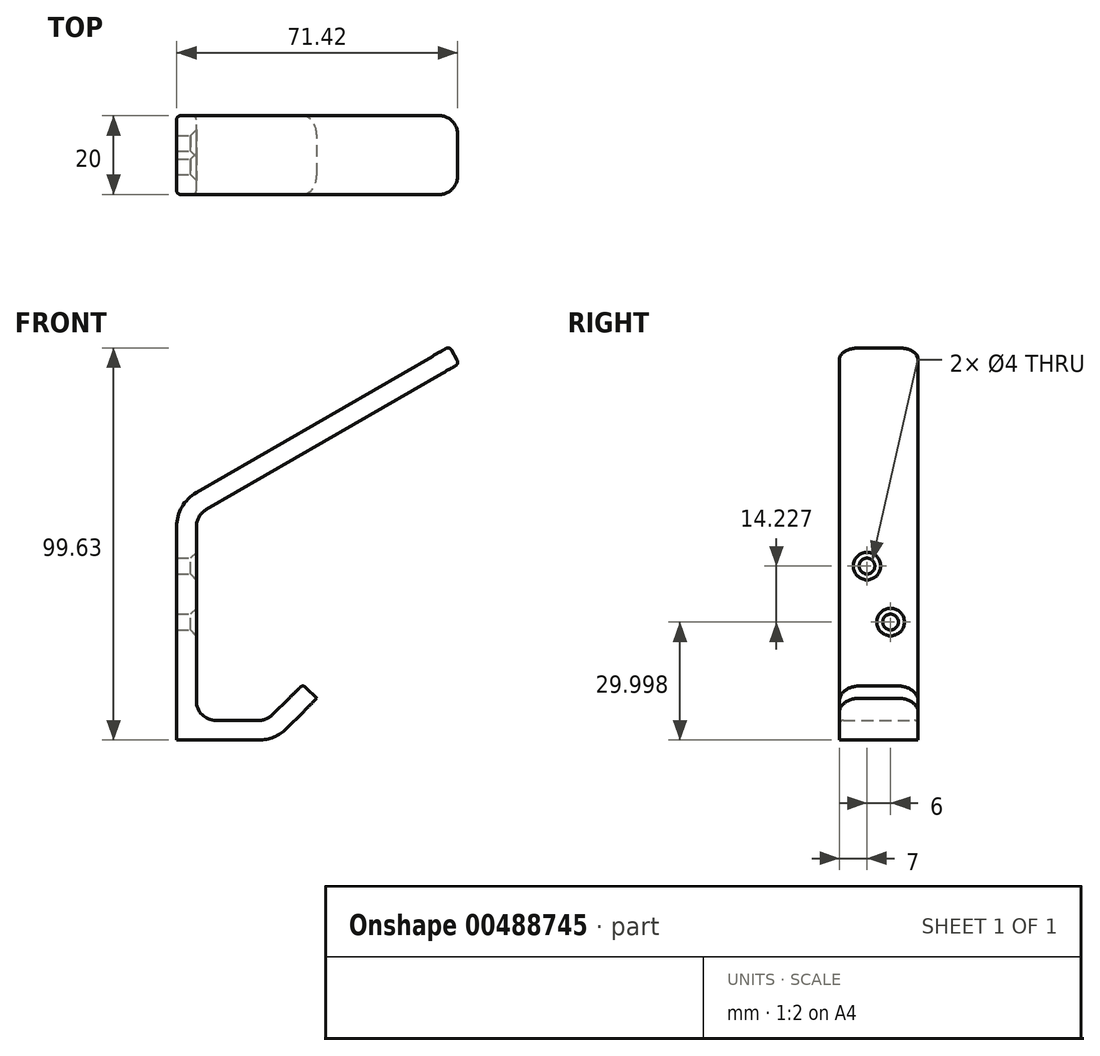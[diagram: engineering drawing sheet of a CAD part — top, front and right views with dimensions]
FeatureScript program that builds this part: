
annotation { "Feature Type Name" : "Feature", "Feature Type Description" : "" }
export const myFeature = defineFeature(function(context is Context, id is Id, definition is map)
    precondition{}
    {
        {
            var Q0;
            Q0=qCreatedBy(makeId("Front.planeOp"),FACE);
            var sketch = newSketch(context, id + "F0", { "sketchPlane" : qUnion([Q0])});
            skLineSegment(sketch, "E0", {"start": v(-35.6, 21.27) * mm, "end": v(-35.6, -38.73) * mm});
            skLineSegment(sketch, "E1", {"start": v(-35.6, 21.27) * mm, "end": v(33.68, 61.27) * mm});
            skLineSegment(sketch, "E2", {"start": v(-35.6, -38.73) * mm, "end": v(-10.6, -38.73) * mm});
            skLineSegment(sketch, "E3", {"start": v(-10.6, -38.73) * mm, "end": v(0, -28.13) * mm});
            skLineSegment(sketch, "E4", {"start": v(0, -28.13) * mm, "end": v(-3.54, -24.59) * mm});
            skLineSegment(sketch, "E5", {"start": v(-3.54, -24.59) * mm, "end": v(-12.68, -33.73) * mm});
            skLineSegment(sketch, "E6", {"start": v(-35.6, -38.73) * mm, "end": v(-35.6, -33.73) * mm});
            skLineSegment(sketch, "E7", {"start": v(-30.6, -33.73) * mm, "end": v(-12.68, -33.73) * mm});
            skLineSegment(sketch, "E8", {"start": v(-35.6, -38.73) * mm, "end": v(-30.6, -38.73) * mm});
            skLineSegment(sketch, "E9", {"start": v(-30.6, -33.73) * mm, "end": v(-30.6, 18.38) * mm});
            skLineSegment(sketch, "E10", {"start": v(33.68, 61.27) * mm, "end": v(36.18, 56.94) * mm});
            skLineSegment(sketch, "E11", {"start": v(36.18, 56.94) * mm, "end": v(-30.6, 18.38) * mm});
            skSolve(sketch);
        }
        {
            var Q0;
            Q0=makeQuery(id+"F0.imprint","IMPRINT",FACE,{"disambiguationData":[TD([[makeQuery(id+"F0.imprint","IMPRINT",EDGE,{"derivedFrom":sQuery(id+"F0.wireOp",EDGE,"E0")}),1.0]])]});
            extrude(context, id + "F1", {"entities" : qUnion([Q0]), "depth" : 20 * mm});
        }
        {
            var Q0;
            Q0=makeQuery(id+"F1.opExtrude","SWEPT_EDGE",EDGE,{"disambiguationData":[OSD([sQuery(id+"F0.wireOp",EDGE,"E0"),sQuery(id+"F0.wireOp",EDGE,"E1")])]});
            fillet(context, id + "F2", {"entities" : qUnion([Q0]), "radius" : 10 * mm, "tangentPropagation" : true, "allowEdgeOverflow" : false});
        }
        {
            var Q0;
            Q0=makeQuery(id+"F1.opExtrude","SWEPT_EDGE",EDGE,{"disambiguationData":[OSD([sQuery(id+"F0.wireOp",EDGE,"E6"),sQuery(id+"F0.wireOp",EDGE,"E8")])]});
            var Q1;
            Q1=makeQuery(id+"F1.opExtrude","SWEPT_EDGE",EDGE,{"disambiguationData":[OSD([sQuery(id+"F0.wireOp",EDGE,"E2"),sQuery(id+"F0.wireOp",EDGE,"E3")])]});
            fillet(context, id + "F3", {"entities" : qUnion([Q0, Q1]), "radius" : 10 * mm, "tangentPropagation" : true, "allowEdgeOverflow" : false});
        }
        {
            var Q0;
            Q0=makeQuery(id+"F1.opExtrude","SWEPT_EDGE",EDGE,{"disambiguationData":[OSD([sQuery(id+"F0.wireOp",EDGE,"E7"),sQuery(id+"F0.wireOp",EDGE,"E9")])]});
            var Q1;
            Q1=makeQuery(id+"F1.opExtrude","SWEPT_EDGE",EDGE,{"disambiguationData":[OSD([sQuery(id+"F0.wireOp",EDGE,"E5"),sQuery(id+"F0.wireOp",EDGE,"E7")])]});
            fillet(context, id + "F4", {"entities" : qUnion([Q0, Q1]), "radius" : 5 * mm, "tangentPropagation" : true, "allowEdgeOverflow" : false});
        }
        {
            var Q0;
            Q0=makeQuery(id+"F1.opExtrude","SWEPT_EDGE",EDGE,{"disambiguationData":[OSD([sQuery(id+"F0.wireOp",EDGE,"E9"),sQuery(id+"F0.wireOp",EDGE,"E11")])]});
            fillet(context, id + "F5", {"entities" : qUnion([Q0]), "radius" : 5 * mm, "tangentPropagation" : true, "allowEdgeOverflow" : false});
        }
        {
            var Q0;
            Q0=makeQuery(id+"F1.opExtrude","CAP_EDGE",EDGE,{"disambiguationData":[OSD([sQuery(id+"F0.wireOp",EDGE,"E4")])],"isStart":true});
            var Q1;
            Q1=makeQuery(id+"F1.opExtrude","CAP_EDGE",EDGE,{"disambiguationData":[OSD([sQuery(id+"F0.wireOp",EDGE,"E4")])],"isStart":false});
            fillet(context, id + "F6", {"entities" : qUnion([Q0, Q1]), "radius" : 5 * mm, "tangentPropagation" : true, "allowEdgeOverflow" : false});
        }
        {
            var Q0;
            Q0=makeQuery(id+"F1.opExtrude","CAP_EDGE",EDGE,{"disambiguationData":[OSD([sQuery(id+"F0.wireOp",EDGE,"E10")])],"isStart":true});
            var Q1;
            Q1=makeQuery(id+"F1.opExtrude","CAP_EDGE",EDGE,{"disambiguationData":[OSD([sQuery(id+"F0.wireOp",EDGE,"E10")])],"isStart":false});
            fillet(context, id + "F7", {"entities" : qUnion([Q0, Q1]), "radius" : 5 * mm, "tangentPropagation" : true, "allowEdgeOverflow" : false});
        }
        {
            var Q0;
            Q0=makeQuery(id+"F1.opExtrude","CAP_EDGE",EDGE,{"disambiguationData":[OSD([sQuery(id+"F0.wireOp",EDGE,"E1")])],"isStart":false});
            var Q1;
            Q1=makeQuery(id+"F1.opExtrude","CAP_EDGE",EDGE,{"disambiguationData":[OSD([sQuery(id+"F0.wireOp",EDGE,"E11")])],"isStart":false});
            var Q2;
            Q2=makeQuery(id+"F7.opFillet","BLEND_EDGE",EDGE,{"blendedFrom":[makeQuery(id+"F1.opExtrude","CAP_EDGE",EDGE,{"disambiguationData":[OSD([sQuery(id+"F0.wireOp",EDGE,"E10")])],"isStart":false}),makeQuery(id+"F1.opExtrude","SWEPT_FACE",FACE,{"disambiguationData":[OSD([sQuery(id+"F0.wireOp",EDGE,"E1")])]})],"blendedInto":[makeQuery(id+"F1.opExtrude","SWEPT_FACE",FACE,{"disambiguationData":[OSD([sQuery(id+"F0.wireOp",EDGE,"E1")])]})]});
            var Q3;
            Q3=makeQuery(id+"F7.opFillet","BLEND_EDGE",EDGE,{"blendedFrom":[makeQuery(id+"F1.opExtrude","CAP_EDGE",EDGE,{"disambiguationData":[OSD([sQuery(id+"F0.wireOp",EDGE,"E10")])],"isStart":false}),makeQuery(id+"F1.opExtrude","SWEPT_FACE",FACE,{"disambiguationData":[OSD([sQuery(id+"F0.wireOp",EDGE,"E11")])]})],"blendedInto":[makeQuery(id+"F1.opExtrude","SWEPT_FACE",FACE,{"disambiguationData":[OSD([sQuery(id+"F0.wireOp",EDGE,"E11")])]})]});
            fillet(context, id + "F8", {"entities" : qUnion([Q0, Q1, Q2, Q3]), "radius" : 1 * mm, "tangentPropagation" : true, "allowEdgeOverflow" : false});
        }
        {
            var Q0;
            Q0=makeQuery(id+"F1.opExtrude","SWEPT_FACE",FACE,{"disambiguationData":[OSD([sQuery(id+"F0.wireOp",EDGE,"E9")])]});
            var sketch = newSketch(context, id + "F9", { "sketchPlane" : qUnion([Q0])});
            skPoint(sketch, "E12", {"position": v(-13, 5.5) * mm});
            skPoint(sketch, "E13", {"position": v(-7, -8.73) * mm});
            skSolve(sketch);
        }
        {
            var Q0;
            Q0=sQuery(id+"F9.wireOp",VERTEX,"E12");
            var Q1;
            Q1=sQuery(id+"F9.wireOp",VERTEX,"E13");
            var Q2;
            Q2=makeQuery(id+"F1.opExtrude","SWEPT_BODY",BODY,{"disambiguationData":[OSD([sQuery(id+"F0.wireOp",EDGE,"E0"),sQuery(id+"F0.wireOp",EDGE,"E1"),sQuery(id+"F0.wireOp",EDGE,"E2"),sQuery(id+"F0.wireOp",EDGE,"E3"),sQuery(id+"F0.wireOp",EDGE,"E4"),sQuery(id+"F0.wireOp",EDGE,"E5"),sQuery(id+"F0.wireOp",EDGE,"E6"),sQuery(id+"F0.wireOp",EDGE,"E7"),sQuery(id+"F0.wireOp",EDGE,"E8"),sQuery(id+"F0.wireOp",EDGE,"E9"),sQuery(id+"F0.wireOp",EDGE,"E10"),sQuery(id+"F0.wireOp",EDGE,"E11")])]});
            hole(context, id + "F10", {"style" : HoleStyle.C_SINK, "endStyle" : HoleEndStyle.THROUGH, "holeDiameter" : 4 * mm, "cSinkDiameter" : 7 * mm, "cSinkAngle" : 90 * degree, "isTappedThrough" : true, "tappedDepth" : 12 * mm, "tapClearance" : 3, "locations" : qUnion([Q0, Q1]), "scope" : qUnion([Q2])});
        }
    });
